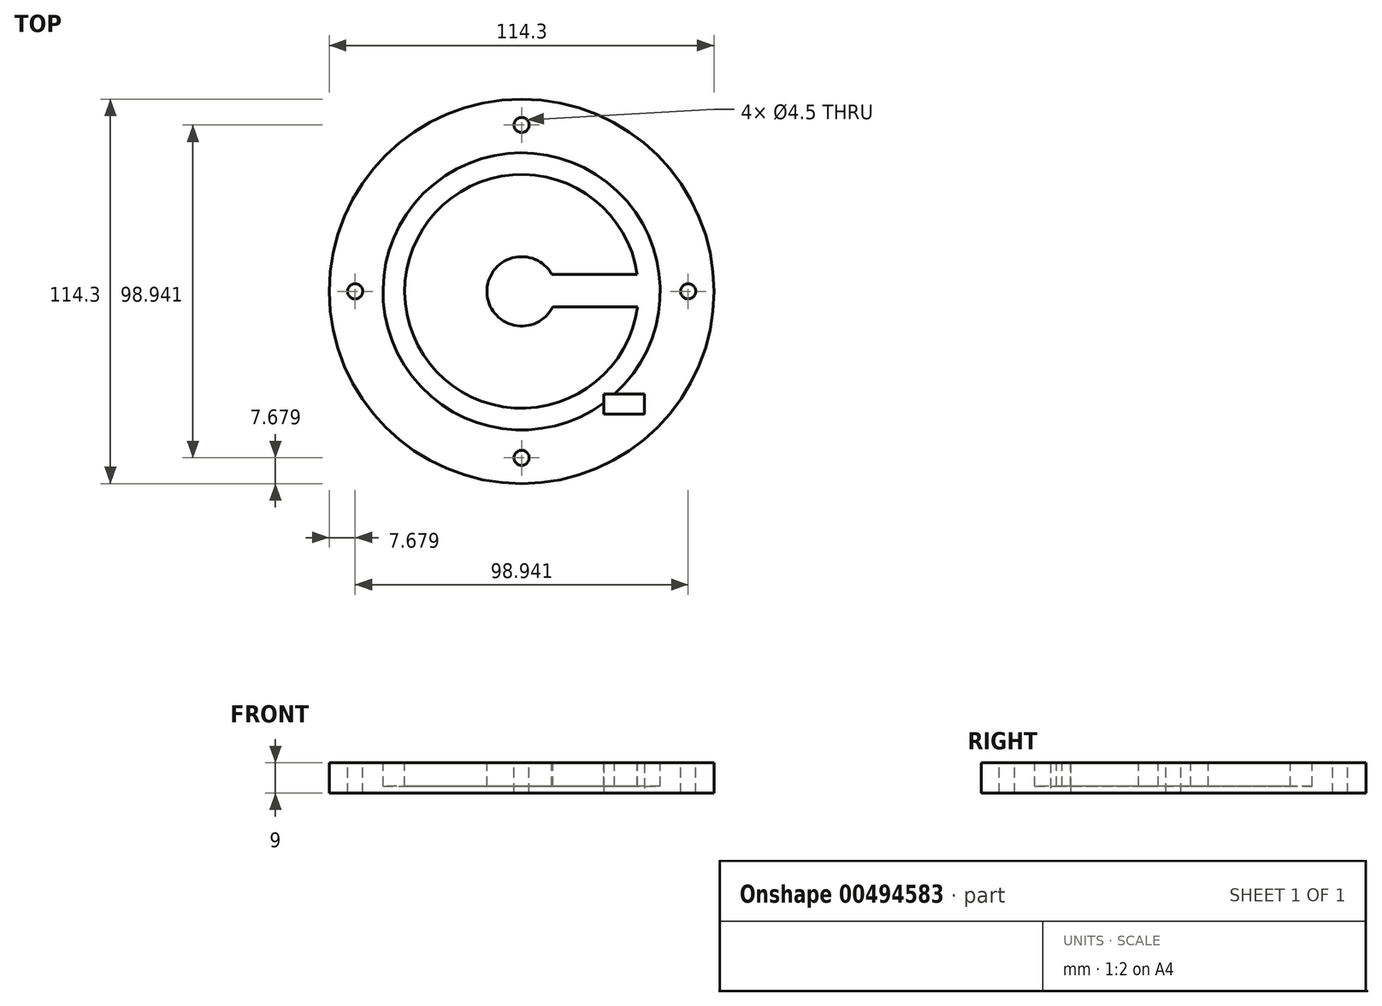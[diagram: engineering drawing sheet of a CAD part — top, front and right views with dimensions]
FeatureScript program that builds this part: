
annotation { "Feature Type Name" : "Feature", "Feature Type Description" : "" }
export const myFeature = defineFeature(function(context is Context, id is Id, definition is map)
    precondition{}
    {
        {
            var Q0;
            Q0=qCreatedBy(makeId("Top.planeOp"),FACE);
            var sketch = newSketch(context, id + "F0", { "sketchPlane" : qUnion([Q0])});
            skCircle(sketch, "E0", {"center": v(0, 0) * mm, "radius": 57.15 * mm});
            skLineSegment(sketch, "E1", {"start": v(0, 0) * mm, "end": v(-90.89, 0) * mm, "construction": true});
            skLineSegment(sketch, "E2", {"start": v(0, 0) * mm, "end": v(91.48, 0) * mm, "construction": true});
            skSolve(sketch);
        }
        {
            var Q0;
            Q0=makeQuery(id+"F0.imprint","IMPRINT",FACE,{"disambiguationData":[TD([[makeQuery(id+"F0.imprint","IMPRINT",EDGE,{"derivedFrom":sQuery(id+"F0.wireOp",EDGE,"E0")}),1.0]])]});
            extrude(context, id + "F1", {"entities" : qUnion([Q0]), "depth" : 9 * mm});
        }
        {
            var Q0;
            Q0=makeQuery(id+"F1.opExtrude","CAP_FACE",FACE,{"disambiguationData":[OSD([sQuery(id+"F0.wireOp",EDGE,"E0")])],"isStart":false});
            var sketch = newSketch(context, id + "F2", { "sketchPlane" : qUnion([Q0])});
            skCircle(sketch, "E3", {"center": v(0, 0) * mm, "radius": 41.18 * mm});
            skCircle(sketch, "E4", {"center": v(0, 0) * mm, "radius": 34.74 * mm});
            skSolve(sketch);
        }
        {
            var Q0;
            Q0=makeQuery(id+"F2.imprint","IMPRINT",FACE,{"disambiguationData":[TD([[makeQuery(id+"F2.imprint","IMPRINT",EDGE,{"derivedFrom":sQuery(id+"F2.wireOp",EDGE,"E3")}),1.0]])]});
            extrude(context, id + "F3", {"entities" : qUnion([Q0]), "operationType" : NewBodyOperationType.REMOVE, "oppositeDirection" : true, "depth" : 7 * mm});
        }
        {
            var Q0;
            Q0=makeQuery(id+"F3.boolean.opBoolean","SPLIT",FACE,{"disambiguationData":[TD([makeQuery(id+"F3.opExtrude","SWEPT_FACE",FACE,{"disambiguationData":[OSD([sQuery(id+"F2.wireOp",EDGE,"E4")])]})])],"derivedFrom":makeQuery(id+"F1.opExtrude","CAP_FACE",FACE,{"disambiguationData":[OSD([sQuery(id+"F0.wireOp",EDGE,"E0")])],"isStart":false})});
            var sketch = newSketch(context, id + "F4", { "sketchPlane" : qUnion([Q0])});
            skCircle(sketch, "E5", {"center": v(0, 0) * mm, "radius": 10.31 * mm});
            skLineSegment(sketch, "E6.bottom", {"start": v(8.97, 5.07) * mm, "end": v(37.77, 5.07) * mm});
            skLineSegment(sketch, "E6.top", {"start": v(8.97, -4.58) * mm, "end": v(37.77, -4.58) * mm});
            skLineSegment(sketch, "E6.left", {"start": v(8.97, 5.07) * mm, "end": v(8.97, -4.58) * mm});
            skLineSegment(sketch, "E6.right", {"start": v(37.77, 5.07) * mm, "end": v(37.77, -4.58) * mm});
            skSolve(sketch);
        }
        {
            var Q0;
            {var subQ0=sQuery(id+"F4.wireOp",EDGE,"E6.left");Q0=makeQuery(id+"F4.imprint","IMPRINT",FACE,{"disambiguationData":[TD([[makeQuery(id+"F4.imprint","IMPRINT",EDGE,{"derivedFrom":subQ0}),1.0]])]});}
            var Q1;
            {var subQ0=sQuery(id+"F4.wireOp",EDGE,"E6.right");Q1=makeQuery(id+"F4.imprint","IMPRINT",FACE,{"disambiguationData":[TD([[makeQuery(id+"F4.imprint","IMPRINT",EDGE,{"derivedFrom":subQ0}),-1.0]])]});}
            var Q2;
            {var subQ0=sQuery(id+"F4.wireOp",EDGE,"E6.left");Q2=makeQuery(id+"F4.imprint","IMPRINT",FACE,{"disambiguationData":[TD([[makeQuery(id+"F4.imprint","IMPRINT",EDGE,{"derivedFrom":subQ0}),-1.0]])]});}
            var Q3;
            {var subQ1=sQuery(id+"F4.wireOp",EDGE,"E5");var subQ3=sQuery(id+"F4.wireOp",EDGE,"E6.top");var subQ4=makeQuery(id+"F4.imprint","INTERSECT",VERTEX,{"derivedFrom":[subQ1,subQ3]});Q3=makeQuery(id+"F4.imprint","IMPRINT",FACE,{"disambiguationData":[TD([[makeQuery(id+"F4.imprint","IMPRINT",EDGE,{"disambiguationData":[TD([[subQ4,-1.0]])],"derivedFrom":subQ3}),1.0]])]});}
            extrude(context, id + "F5", {"entities" : qUnion([Q0, Q1, Q2, Q3]), "operationType" : NewBodyOperationType.REMOVE, "oppositeDirection" : true, "depth" : 7 * mm});
        }
        {
            var Q0;
            Q0=makeQuery(id+"F1.opExtrude","CAP_FACE",FACE,{"disambiguationData":[OSD([sQuery(id+"F0.wireOp",EDGE,"E0")])],"isStart":true});
            var sketch = newSketch(context, id + "F6", { "sketchPlane" : qUnion([Q0])});
            skLineSegment(sketch, "E7.bottom", {"start": v(24.43, 36.54) * mm, "end": v(36.43, 36.54) * mm});
            skLineSegment(sketch, "E7.top", {"start": v(24.43, 30.54) * mm, "end": v(36.43, 30.54) * mm});
            skLineSegment(sketch, "E7.left", {"start": v(24.43, 36.54) * mm, "end": v(24.43, 30.54) * mm});
            skLineSegment(sketch, "E7.right", {"start": v(36.43, 36.54) * mm, "end": v(36.43, 30.54) * mm});
            skSolve(sketch);
        }
        {
            var Q0;
            Q0 = qSketchRegion(id + "F6", true);
            extrude(context, id + "F7", {"entities" : qUnion([Q0]), "operationType" : NewBodyOperationType.REMOVE, "oppositeDirection" : true, "depth" : 9 * mm});
        }
        {
            var Q0;
            {var subQ0=sQuery(id+"F0.wireOp",EDGE,"E0");Q0=makeQuery(id+"F3.boolean.opBoolean","SPLIT",FACE,{"disambiguationData":[TD([makeQuery(id+"F1.opExtrude","SWEPT_FACE",FACE,{"disambiguationData":[OSD([subQ0])]})])],"derivedFrom":makeQuery(id+"F1.opExtrude","CAP_FACE",FACE,{"disambiguationData":[OSD([subQ0])],"isStart":false})});}
            var sketch = newSketch(context, id + "F8", { "sketchPlane" : qUnion([Q0])});
            skCircle(sketch, "E8", {"center": v(0, 0) * mm, "radius": 49.47 * mm});
            skPoint(sketch, "E9", {"position": v(0, 49.47) * mm});
            skPoint(sketch, "E10", {"position": v(0, -49.47) * mm});
            skPoint(sketch, "E11", {"position": v(49.47, 0) * mm});
            skPoint(sketch, "E12", {"position": v(-49.47, 0) * mm});
            skSolve(sketch);
        }
        {
            var Q0;
            Q0=sQuery(id+"F8.wireOp",VERTEX,"E9");
            var Q1;
            Q1=sQuery(id+"F8.wireOp",VERTEX,"E12");
            var Q2;
            Q2=sQuery(id+"F8.wireOp",VERTEX,"E10");
            var Q3;
            Q3=sQuery(id+"F8.wireOp",VERTEX,"E11");
            var Q4;
            Q4=makeQuery(id+"F1.opExtrude","SWEPT_BODY",BODY,{"disambiguationData":[OSD([sQuery(id+"F0.wireOp",EDGE,"E0")])]});
            hole(context, id + "F9", {"style" : HoleStyle.SIMPLE, "endStyle" : HoleEndStyle.THROUGH, "standardTappedOrClearance" : lookupTablePath({ "standard" : "ANSI", "fit" : "Normal (ASME)", "size" : "#8", "type" : "Clearance" }), "standardBlindInLast" : lookupTablePath({ "fit" : "Free", "standard" : "ANSI", "size" : "#8", "type" : "Clearance" }), "holeDiameter" : 4.5 * mm, "isTappedThrough" : true, "tappedDepth" : 12.7 * mm, "tapClearance" : 3, "locations" : qUnion([Q0, Q1, Q2, Q3]), "scope" : qUnion([Q4])});
        }
    });
